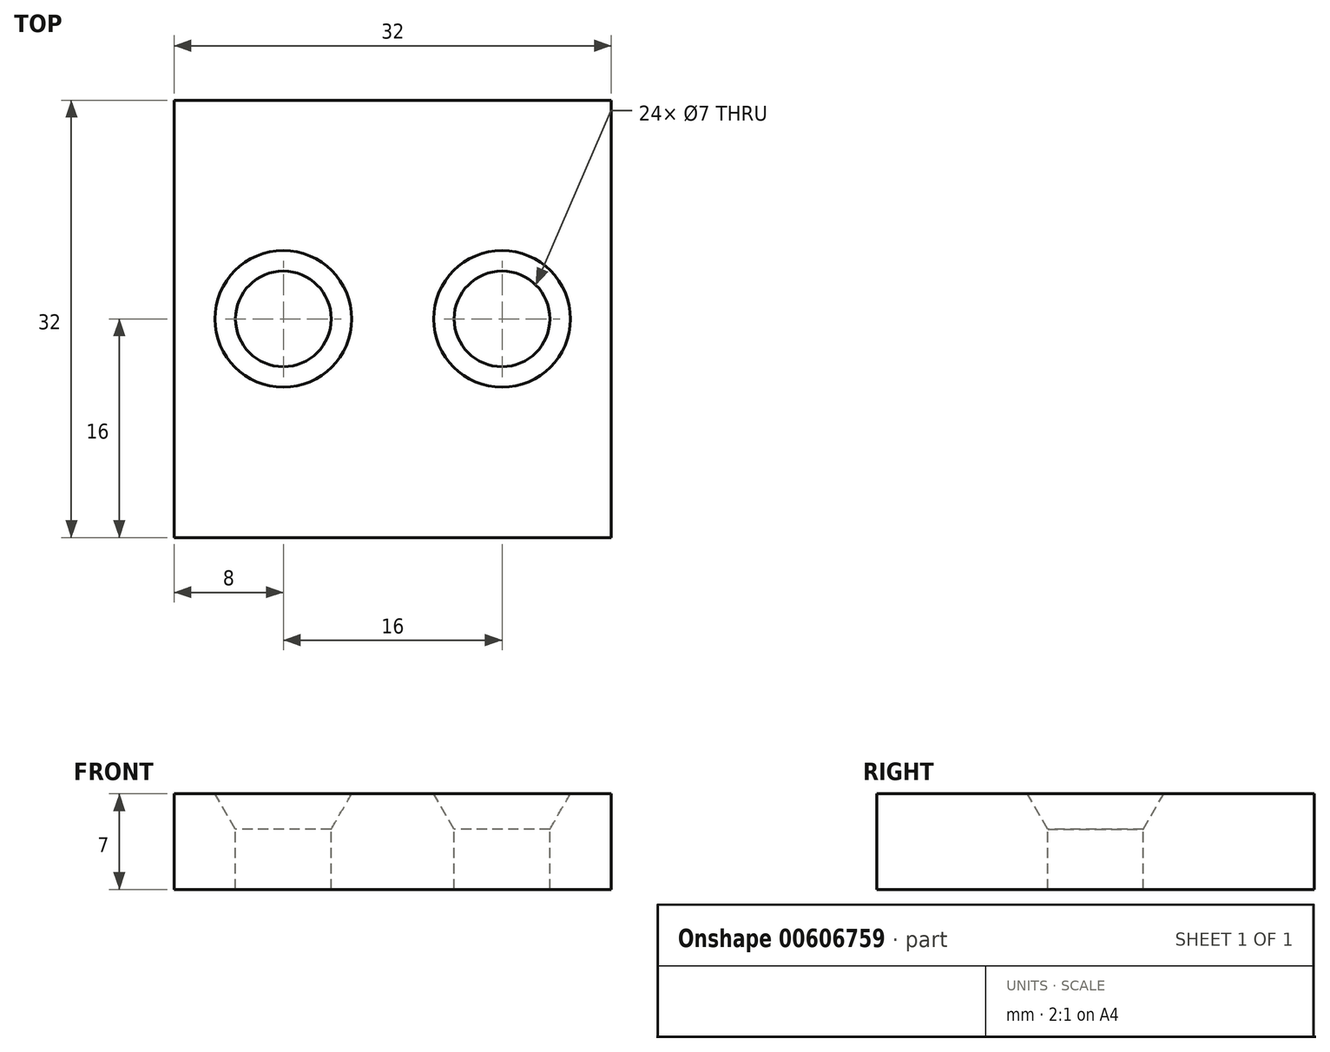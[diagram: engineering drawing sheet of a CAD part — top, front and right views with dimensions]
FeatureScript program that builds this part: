
annotation { "Feature Type Name" : "Feature", "Feature Type Description" : "" }
export const myFeature = defineFeature(function(context is Context, id is Id, definition is map)
    precondition{}
    {
        {
            var Q0;
            Q0=qCreatedBy(makeId("Top.planeOp"),FACE);
            var sketch = newSketch(context, id + "F0", { "sketchPlane" : qUnion([Q0])});
            skLineSegment(sketch, "E0.bottom", {"start": v(16, 16) * mm, "end": v(-16, 16) * mm});
            skLineSegment(sketch, "E0.top", {"start": v(16, -16) * mm, "end": v(-16, -16) * mm});
            skLineSegment(sketch, "E0.left", {"start": v(16, 16) * mm, "end": v(16, -16) * mm});
            skLineSegment(sketch, "E0.right", {"start": v(-16, 16) * mm, "end": v(-16, -16) * mm});
            skPoint(sketch, "E0.middle", {"position": v(0, 0) * mm});
            skSolve(sketch);
        }
        {
            var Q0;
            Q0 = qSketchRegion(id + "F0", true);
            extrude(context, id + "F1", {"entities" : qUnion([Q0]), "depth" : 7 * mm, "offsetDistance" : 25 * mm});
        }
        {
            var Q0;
            Q0=makeQuery(id+"F1.opExtrude","CAP_FACE",FACE,{"disambiguationData":[OSD([sQuery(id+"F0.wireOp",EDGE,"E0.bottom"),sQuery(id+"F0.wireOp",EDGE,"E0.top"),sQuery(id+"F0.wireOp",EDGE,"E0.left"),sQuery(id+"F0.wireOp",EDGE,"E0.right")])],"isStart":false});
            var sketch = newSketch(context, id + "F2", { "sketchPlane" : qUnion([Q0])});
            skPoint(sketch, "E1", {"position": v(-8, 0) * mm});
            skPoint(sketch, "E2", {"position": v(8, 0) * mm});
            skSolve(sketch);
        }
        {
            var Q0;
            Q0=sQuery(id+"F2.wireOp",VERTEX,"E1");
            var Q1;
            Q1=sQuery(id+"F2.wireOp",VERTEX,"E2");
            var Q2;
            Q2=makeQuery(id+"F1.opExtrude","SWEPT_BODY",BODY,{"disambiguationData":[OSD([sQuery(id+"F0.wireOp",EDGE,"E0.bottom"),sQuery(id+"F0.wireOp",EDGE,"E0.top"),sQuery(id+"F0.wireOp",EDGE,"E0.left"),sQuery(id+"F0.wireOp",EDGE,"E0.right")])]});
            hole(context, id + "F3", {"style" : HoleStyle.C_SINK, "endStyle" : HoleEndStyle.THROUGH, "holeDiameter" : 7 * mm, "cSinkDiameter" : 10 * mm, "cSinkAngle" : 60 * degree, "majorDiameter" : 5 * mm, "isTappedThrough" : true, "tappedDepth" : 12 * mm, "tapClearance" : 3, "startFromSketch" : true, "locations" : qUnion([Q0, Q1]), "scope" : qUnion([Q2])});
        }
    });
